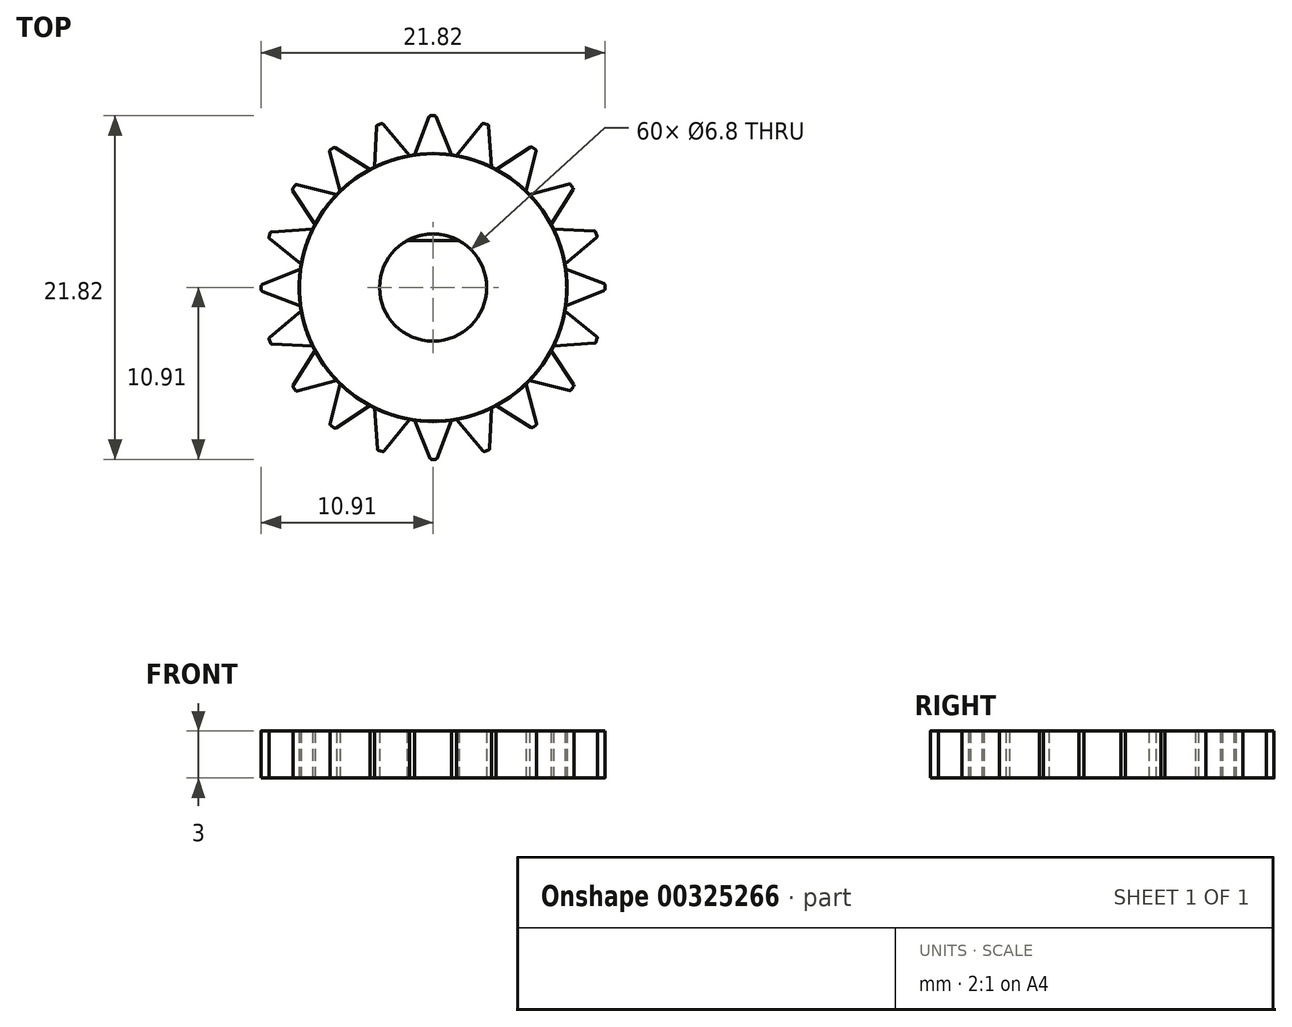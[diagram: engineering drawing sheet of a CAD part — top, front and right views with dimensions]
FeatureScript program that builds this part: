
annotation { "Feature Type Name" : "Feature", "Feature Type Description" : "" }
export const myFeature = defineFeature(function(context is Context, id is Id, definition is map)
    precondition{}
    {
        {
            var Q0;
            Q0=qCreatedBy(makeId("Top.planeOp"),FACE);
            var sketch = newSketch(context, id + "F0", { "sketchPlane" : qUnion([Q0])});
            skCircle(sketch, "E0", {"center": v(0, 0) * mm, "radius": 8.5 * mm});
            skCircle(sketch, "E1", {"center": v(0, 0) * mm, "radius": 11.5 * mm});
            skCircle(sketch, "E2", {"center": v(0, 0) * mm, "radius": 3.4 * mm});
            skLineSegment(sketch, "E3", {"start": v(-1.65, 2.97) * mm, "end": v(1.65, 2.97) * mm});
            skLineSegment(sketch, "E4", {"start": v(-0.25, 10.85) * mm, "end": v(-1.18, 8.42) * mm});
            skLineSegment(sketch, "E5", {"start": v(0.2, 10.85) * mm, "end": v(1.18, 8.42) * mm});
            skLineSegment(sketch, "E6", {"start": v(-0.16, 10.9) * mm, "end": v(0.1, 10.9) * mm});
            skPoint(sketch, "E7.newPointA", {"position": v(0, 11.5) * mm});
            skArc(sketch, "E7.filletArc", {"start": v(-0.16, 10.9) * mm, "mid": v(-0.21, 10.9) * mm, "end": v(-0.25, 10.85) * mm});
            skPoint(sketch, "E8.newPointA", {"position": v(-0.06, 11.48) * mm});
            skArc(sketch, "E8.filletArc", {"start": v(0.2, 10.85) * mm, "mid": v(0.16, 10.9) * mm, "end": v(0.1, 10.9) * mm});
            skSolve(sketch);
        }
        {
            var Q0;
            {var subQ0=sQuery(id+"F0.wireOp",EDGE,"E0");var subQ1=makeQuery(id+"F0.imprint","INTERSECT",VERTEX,{"derivedFrom":[subQ0,sQuery(id+"F0.wireOp",EDGE,"amzuy7TR-VJov-cKzR-yEhH-5YaXYhgMwhYQ")]});Q0=makeQuery(id+"F0.imprint","IMPRINT",FACE,{"disambiguationData":[TD([[makeQuery(id+"F0.imprint","IMPRINT",EDGE,{"disambiguationData":[TD([[subQ1,1.0]])],"derivedFrom":subQ0}),1.0]])]});}
            var Q1;
            {var subQ0=sQuery(id+"F0.wireOp",EDGE,"amzuy7TR-VJov-cKzR-yEhH-5YaXYhgMwhYQ");Q1=makeQuery(id+"F0.imprint","IMPRINT",FACE,{"disambiguationData":[TD([[makeQuery(id+"F0.imprint","IMPRINT",EDGE,{"derivedFrom":subQ0}),1.0]])]});}
            var Q2;
            {var subQ0=sQuery(id+"F0.wireOp",EDGE,"E4");Q2=makeQuery(id+"F0.imprint","IMPRINT",FACE,{"disambiguationData":[TD([[makeQuery(id+"F0.imprint","IMPRINT",EDGE,{"derivedFrom":subQ0}),1.0]])]});}
            extrude(context, id + "F1", {"entities" : qUnion([Q0, Q1, Q2]), "depth" : 3 * mm});
        }
        {
            var Q0;
            Q0=qCreatedBy(makeId("Right.planeOp"),FACE);
            var sketch = newSketch(context, id + "F2", { "sketchPlane" : qUnion([Q0])});
            skLineSegment(sketch, "E9", {"start": v(0, 0) * mm, "end": v(0, 21.76) * mm});
            skSolve(sketch);
        }
        {
            var Q0;
            Q0=makeQuery(id+"F1.opExtrude","SWEPT_BODY",BODY,{"disambiguationData":[OSD([sQuery(id+"F0.wireOp",EDGE,"E0"),sQuery(id+"F0.wireOp",EDGE,"amzuy7TR-VJov-cKzR-yEhH-5YaXYhgMwhYQ"),sQuery(id+"F0.wireOp",EDGE,"uRJDN2hV-OOGK-avrN-CSsd-R0Fi45Zma8uD"),sQuery(id+"F0.wireOp",EDGE,"E2"),sQuery(id+"F0.wireOp",EDGE,"E3")])]});
            var Q1;
            Q1=sQuery(id+"F2.wireOp",EDGE,"E9");
            circularPattern(context, id + "F3", {"entities" : qUnion([Q0]), "axis" : qUnion([Q1]), "angle" : 360 * degree, "instanceCount" : 20, "equalSpace" : true});
        }
        {
            var Q0;
            {var subQ0=sQuery(id+"F0.wireOp",EDGE,"E3");Q0=makeQuery(id+"F0.imprint","IMPRINT",FACE,{"disambiguationData":[TD([[makeQuery(id+"F0.imprint","IMPRINT",EDGE,{"derivedFrom":subQ0}),1.0]])]});}
            extrude(context, id + "F4", {"entities" : qUnion([Q0]), "depth" : 3 * mm});
        }
    });
